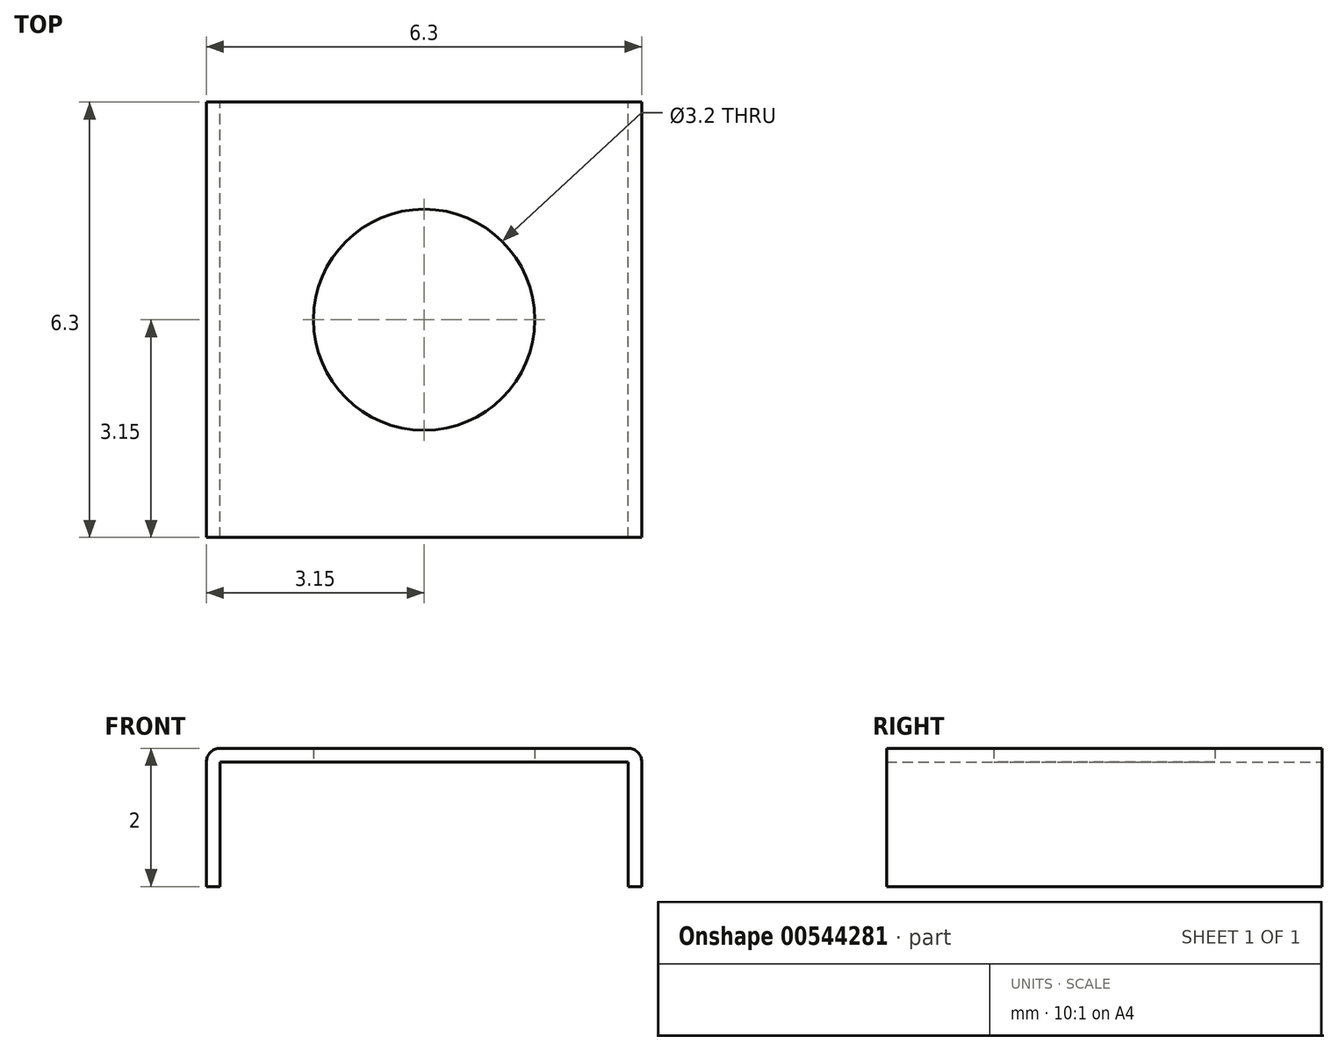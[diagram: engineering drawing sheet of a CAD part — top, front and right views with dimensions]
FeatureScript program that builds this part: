
annotation { "Feature Type Name" : "Feature", "Feature Type Description" : "" }
export const myFeature = defineFeature(function(context is Context, id is Id, definition is map)
    precondition{}
    {
        {
            var Q0;
            Q0=qCreatedBy(makeId("Top.planeOp"),FACE);
            var sketch = newSketch(context, id + "F0", { "sketchPlane" : qUnion([Q0])});
            skLineSegment(sketch, "E0.bottom", {"start": v(0, 0) * mm, "end": v(6.3, 0) * mm});
            skLineSegment(sketch, "E0.top", {"start": v(0, 6.3) * mm, "end": v(6.3, 6.3) * mm});
            skLineSegment(sketch, "E0.left", {"start": v(0, 0) * mm, "end": v(0, 6.3) * mm});
            skLineSegment(sketch, "E0.right", {"start": v(6.3, 0) * mm, "end": v(6.3, 6.3) * mm});
            skCircle(sketch, "E1", {"center": v(3.15, 3.15) * mm, "radius": 1.6 * mm});
            skSolve(sketch);
        }
        {
            var Q0;
            Q0=qSketchRegion(id+"F0",true);
            extrude(context, id + "F1", {"entities" : qUnion([Q0]), "depth" : 0.2 * mm});
        }
        {
            var Q0;
            Q0=makeQuery(id+"F1.opExtrude","CAP_FACE",FACE,{"disambiguationData":[OSD([sQuery(id+"F0.wireOp",EDGE,"E0.bottom"),sQuery(id+"F0.wireOp",EDGE,"E0.top"),sQuery(id+"F0.wireOp",EDGE,"E0.left"),sQuery(id+"F0.wireOp",EDGE,"E0.right"),sQuery(id+"F0.wireOp",EDGE,"E1")])],"isStart":true});
            var sketch = newSketch(context, id + "F2", { "sketchPlane" : qUnion([Q0])});
            skLineSegment(sketch, "E2.bottom", {"start": v(0, 0) * mm, "end": v(0.2, 0) * mm});
            skLineSegment(sketch, "E2.top", {"start": v(0, -6.3) * mm, "end": v(0.2, -6.3) * mm});
            skLineSegment(sketch, "E2.left", {"start": v(0, 0) * mm, "end": v(0, -6.3) * mm});
            skLineSegment(sketch, "E2.right", {"start": v(0.2, 0) * mm, "end": v(0.2, -6.3) * mm});
            skLineSegment(sketch, "E3.bottom", {"start": v(6.3, 0) * mm, "end": v(6.1, 0) * mm});
            skLineSegment(sketch, "E3.top", {"start": v(6.3, -6.3) * mm, "end": v(6.1, -6.3) * mm});
            skLineSegment(sketch, "E3.left", {"start": v(6.3, 0) * mm, "end": v(6.3, -6.3) * mm});
            skLineSegment(sketch, "E3.right", {"start": v(6.1, 0) * mm, "end": v(6.1, -6.3) * mm});
            skSolve(sketch);
        }
        {
            var Q0;
            Q0=qSketchRegion(id+"F2",true);
            extrude(context, id + "F3", {"entities" : qUnion([Q0]), "operationType" : NewBodyOperationType.ADD, "depth" : 1.8 * mm});
        }
        {
            var Q0;
            Q0=makeQuery(id+"F1.opExtrude","CAP_EDGE",EDGE,{"disambiguationData":[OSD([sQuery(id+"F0.wireOp",EDGE,"E0.left")])],"isStart":false});
            var Q1;
            Q1=makeQuery(id+"F1.opExtrude","CAP_EDGE",EDGE,{"disambiguationData":[OSD([sQuery(id+"F0.wireOp",EDGE,"E0.right")])],"isStart":false});
            fillet(context, id + "F4", {"entities" : qUnion([Q0, Q1]), "radius" : 0.2 * mm, "tangentPropagation" : true, "allowEdgeOverflow" : false});
        }
    });
